# Revit family: Hydrant-Wall_Encased_Zurn-Z1330-C_Moderate_Climate
name_source: partatom
category: Plumbing Fixtures
units: mm (PartAtom-declared; Revit-internal decimal feet)

## family parameters
Cut with Voids When Loaded = No
Host = Face
Maintain Annotation Orientation = No
OmniClass Number = 23.65.70.14.11.11
OmniClass Title = Security Drinking Fountains/Coolers
Part Type = Normal
Room Calculation Point = No
Round Connector Dimension = Use Radius
Shared = No

## types (1)
- 8 Inch Wall Thickness
    3/4 Inlet Female Solder and Male Threaded = 0.375 "
    3/4 Outlet Hose Connection = 0.375 "
    Approx. Wt. Lbs. = 0 "
    Assembly Code = D2020100
    Box and Cover = Steel - Zurn Industries - Stainless Type 304
    CW Connection = Yes
    CWFU = 1
    Default Elevation = 48 "
    Depth = 6.5 "
    Description = Moderate Climate Encased Wall Hydrant
    Female Solder and Male Pipe Thread = 0 GPM
    HW Connection = No
    HWFU = 0
    Head and Valve Housing = Bronze - Zurn Industries, LLC - Cast
    Length = 6.5 "
    Manufacturer = Zurn Water, LLC
    Model = Z1330-C
    Modified Date = 09/05/2025
    Product Documentation Link = http://content.zurn.com
    Product Page URL = http://www.zurn.com
    Product data url = https://bimobject.com
    URL = www.zurn.com
    Vent Connection = No
    WFU = 0
    Waste Connection = No
    Width = 6.5 "

## geometry (parser evidence)
native form markers: Blend x51, Sweep x2
no freeform markers — native parametric forms only
